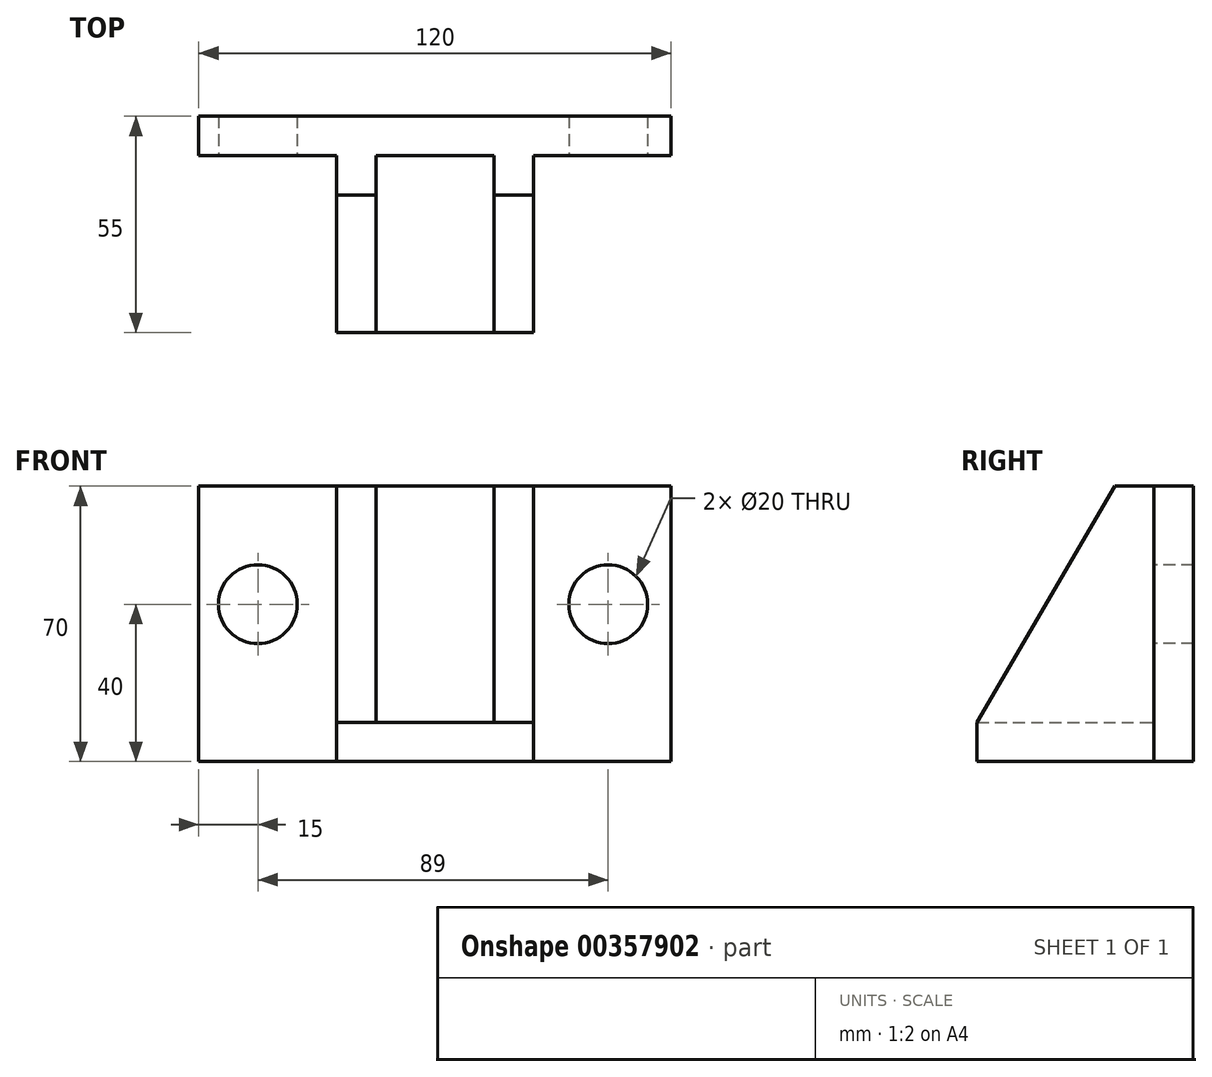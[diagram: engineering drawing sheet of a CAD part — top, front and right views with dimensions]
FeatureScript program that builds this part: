
annotation { "Feature Type Name" : "Feature", "Feature Type Description" : "" }
export const myFeature = defineFeature(function(context is Context, id is Id, definition is map)
    precondition{}
    {
        {
            var Q0;
            Q0=qCreatedBy(makeId("Front.planeOp"),FACE);
            var sketch = newSketch(context, id + "F0", { "sketchPlane" : qUnion([Q0])});
            skLineSegment(sketch, "E0.bottom", {"start": v(-60, 35) * mm, "end": v(60, 35) * mm});
            skLineSegment(sketch, "E0.top", {"start": v(-60, -35) * mm, "end": v(60, -35) * mm});
            skLineSegment(sketch, "E0.left", {"start": v(-60, 35) * mm, "end": v(-60, -35) * mm});
            skLineSegment(sketch, "E0.right", {"start": v(60, 35) * mm, "end": v(60, -35) * mm});
            skPoint(sketch, "E0.middle", {"position": v(0, 0) * mm});
            skSolve(sketch);
        }
        {
            var Q0;
            Q0 = qSketchRegion(id + "F0", true);
            extrude(context, id + "F1", {"entities" : qUnion([Q0]), "depth" : 10 * mm});
        }
        {
            var Q0;
            Q0=makeQuery(id+"F1.opExtrude","CAP_FACE",FACE,{"disambiguationData":[OSD([sQuery(id+"F0.wireOp",EDGE,"E0.bottom"),sQuery(id+"F0.wireOp",EDGE,"E0.top"),sQuery(id+"F0.wireOp",EDGE,"E0.left"),sQuery(id+"F0.wireOp",EDGE,"E0.right")])],"isStart":false});
            var sketch = newSketch(context, id + "F2", { "sketchPlane" : qUnion([Q0])});
            skCircle(sketch, "E1", {"center": v(-45, 5) * mm, "radius": 10 * mm});
            skCircle(sketch, "E2", {"center": v(44, 5) * mm, "radius": 10 * mm});
            skLineSegment(sketch, "E3.bottom", {"start": v(-25, 35) * mm, "end": v(-15, 35) * mm});
            skLineSegment(sketch, "E3.top", {"start": v(-25, -35) * mm, "end": v(-15, -35) * mm});
            skLineSegment(sketch, "E3.left", {"start": v(-25, 35) * mm, "end": v(-25, -35) * mm});
            skLineSegment(sketch, "E3.right", {"start": v(-15, 35) * mm, "end": v(-15, -25) * mm});
            skLineSegment(sketch, "E4.bottom", {"start": v(25, 35) * mm, "end": v(15, 35) * mm});
            skLineSegment(sketch, "E4.top", {"start": v(25, -35) * mm, "end": v(15, -35) * mm});
            skLineSegment(sketch, "E4.left", {"start": v(25, 35) * mm, "end": v(25, -35) * mm});
            skLineSegment(sketch, "E4.right", {"start": v(15, 35) * mm, "end": v(15, -25) * mm});
            skLineSegment(sketch, "E5.bottom", {"start": v(-25, -35) * mm, "end": v(25, -35) * mm});
            skLineSegment(sketch, "E5.top", {"start": v(-15, -25) * mm, "end": v(15, -25) * mm});
            skLineSegment(sketch, "E5.left", {"start": v(-25, -35) * mm, "end": v(-25, -25) * mm});
            skLineSegment(sketch, "E5.right", {"start": v(25, -35) * mm, "end": v(25, -25) * mm});
            skSolve(sketch);
        }
        {
            var Q0;
            Q0=makeQuery(id+"F2.imprint","IMPRINT",FACE,{"disambiguationData":[TD([[makeQuery(id+"F2.imprint","IMPRINT",EDGE,{"derivedFrom":sQuery(id+"F2.wireOp",EDGE,"E1")}),1.0]])]});
            var Q1;
            Q1=makeQuery(id+"F2.imprint","IMPRINT",FACE,{"disambiguationData":[TD([[makeQuery(id+"F2.imprint","IMPRINT",EDGE,{"derivedFrom":sQuery(id+"F2.wireOp",EDGE,"E2")}),1.0]])]});
            var Q2;
            Q2=sQuery(id+"F2.wireOp",EDGE,"E1");
            var Q3;
            Q3=sQuery(id+"F2.wireOp",EDGE,"E2");
            extrude(context, id + "F3", {"entities" : qUnion([Q0, Q1]), "operationType" : NewBodyOperationType.REMOVE, "surfaceEntities" : qUnion([Q2, Q3]), "endBound" : BoundingType.THROUGH_ALL, "oppositeDirection" : true, "depth" : 25 * mm});
        }
        {
            var Q0;
            Q0=makeQuery(id+"F2.imprint","IMPRINT",FACE,{"disambiguationData":[TD([[makeQuery(id+"F2.imprint","IMPRINT",EDGE,{"derivedFrom":sQuery(id+"F2.wireOp",EDGE,"E3.bottom")}),-1.0]])]});
            extrude(context, id + "F4", {"entities" : qUnion([Q0]), "operationType" : NewBodyOperationType.ADD, "depth" : 45 * mm});
        }
        {
            var Q0;
            Q0=makeQuery(id+"F4.opExtrude","SWEPT_FACE",FACE,{"disambiguationData":[OSD([sQuery(id+"F2.wireOp",EDGE,"E4.left"),sQuery(id+"F2.wireOp",EDGE,"E5.right")])]});
            var sketch = newSketch(context, id + "F5", { "sketchPlane" : qUnion([Q0])});
            skLineSegment(sketch, "E6", {"start": v(-20, 35) * mm, "end": v(-55, 35) * mm});
            skLineSegment(sketch, "E7", {"start": v(-55, 35) * mm, "end": v(-55, -25) * mm});
            skLineSegment(sketch, "E8", {"start": v(-55, -25) * mm, "end": v(-20, 35) * mm});
            skSolve(sketch);
        }
        {
            var Q0;
            Q0 = qSketchRegion(id + "F5", true);
            var Q1;
            Q1=makeQuery(id+"F4.opExtrude","SWEPT_FACE",FACE,{"disambiguationData":[OSD([sQuery(id+"F2.wireOp",EDGE,"E3.left"),sQuery(id+"F2.wireOp",EDGE,"E5.left")])]});
            extrude(context, id + "F6", {"entities" : qUnion([Q0]), "operationType" : NewBodyOperationType.REMOVE, "endBound" : BoundingType.UP_TO_SURFACE, "oppositeDirection" : true, "endBoundEntityFace" : qUnion([Q1]), "depth" : 25 * mm});
        }
    });
